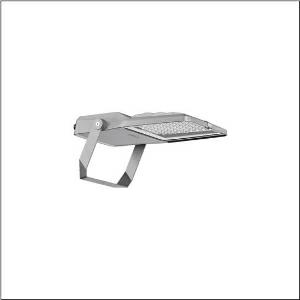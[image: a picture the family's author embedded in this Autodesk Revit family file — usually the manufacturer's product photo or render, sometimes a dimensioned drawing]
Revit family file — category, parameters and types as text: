
# Revit family: floodlight_fl_21_mini___pl64_5xa7772b3e1a_8f62
name_source: partatom
category: Lighting Fixtures
units: mm (PartAtom-declared; Revit-internal decimal feet)

## family parameters
Cut with Voids When Loaded = No
Host = Face
Light Source = No
Part Type = Normal
Room Calculation Point = No
Round Connector Dimension = Use Diameter
Shared = No

## types (1)
- --- (1 x LED, 5190 lm, 45.5 W, 3000K)
    Apparent Load = 46 VA
    CIE Flux Codes = 28 80 98 100 100
    Color Rendering = 80
    Color Temperature = 3000K
    Default Elevation = 1800 mm
    Description = Floodlight FL 21 mini, floodlight, primary light control with lens, of PMMA, primary optical cover: protective disc, of toughened safety glass, transparent, light distribution: PL64, light emission: direct distribution, installation type: surface-mounted, LED, High Power LED, rated luminous flux: 5.190lm, luminous efficacy: 114lm/W, light colour: 830, colour temperature: 3000K, control gear: ECG iQ, control: Street-Remote, Auto-Match, Temp-Guard, Night-Set, Smart-Wire, Desk-Remote (wireless, voltage-free reading and setting of iQ features in the workshop via application-optimized NFC function/RFID function), optimised constant luminous flux control (CLO 2.0), with terminal, 6-pole, mains connection: 220..240V, AC, 50/60Hz, start of lifetime: 46W, end of lifetime: 48W, reduction: 21W, luminaire housing, of diecast aluminium, powder-coated, Siteco® metallic grey (DB 702S), corrosivity category C5 according to DIN EN ISO 12944, mounting bracket, of steel, galvanised, powder-coated, Siteco® metallic grey (DB 702S), protection rating (complete): IP66, insulation class (complete): insulation class II (safety insulation), certification: CE, ENEC, VDE, protection symbol: D, impact resistance: IK08, permissible operating ambient temperature: -40..+40°C, permissible operating ambient temperature for outdoor applications: -40..+50°C, standard: DIN EN 12944, packaging unit: 1 piece

Light Distribution: PL64
    Height = 70 mm
    Lamp = 1 x LED
    Lamp Light Flux = 5190 lm
    Lamp Power = 45.5 W
    Lamp count = 1
    Length = 485 mm
    Luminous efficacy = 114 lm/W
    Manufacturer = Siteco
    ModVariant = No
    Model = 5XA7772B3E1A
    Number of Poles = 1
    OnlyDefault = Yes
    Power Factor = 1
    Product Name = Floodlight FL 21 mini | PL64
    Product group = floodlight | pylon top
    ProductGroupID = 6101
    Protection Class = Protection class II
    Protection Degree = IP 66
    RLX_Detail_Level = 1
    RlxData = <blob elided: 96041 chars, md5=6167d1fe>
    Socket = socket
    Standby Power = 0 W
    System Light Flux = 5190 lm
    System Power = 46 W
    Type Comments = factory setting: luminous flux: 100 % | dim-lin: 254 | 463 mA
    Type Image = l_1006845.jpg
    URL = http://relux.com
    VarID = @adj_077917
    Voltage = 0 V
    Weight = 0.00 kg
    Width = 337 mm

## geometry (parser evidence)
native form markers: Blend x4, Sweep x11
no freeform markers — native parametric forms only
